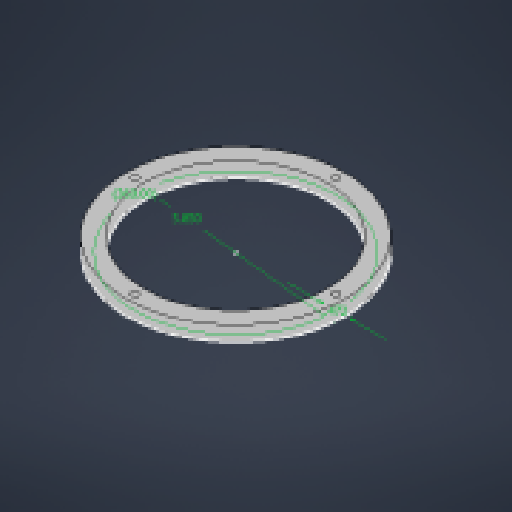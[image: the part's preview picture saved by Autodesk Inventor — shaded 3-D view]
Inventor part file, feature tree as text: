
AUTODESK INVENTOR PART (.ipt)
format: ipt  version: 2024 (Build 280153000, 153)  size: 141,312 bytes
history: native  units: in
note: dims shown in document units (in); Inventor stores cm internally (conversion verified against a paired STEP export)
features: sketch x1, extrude x1, hole x1
ambient origin geometry x8: Origin, YZ Plane, XZ Plane, XY Plane, X Axis, Y Axis, Z Axis, Center Point
bodies: Solid1 (feature_tree)
feature tree (3):
  sketch  "Sketch1"  dims[d0=5.8504in d1=0.4724in d2=1.5748in d4=360.0deg d6=0.3937in d7=0.0in d8=0.1969in d9=0.394in d10=0.409in d11=0.25in d12=90.0deg d13=1.0in d14=0.8108in]
  extrude  "Extrusion1"  Depth=0.3937in
  hole  "Hole1"  [1 undecoded]
note: 1 required parameter value undecoded (feature->parameter linkage not recoverable at this tier; creation-order binding heuristic only, values carry confidence <= 0.55)
